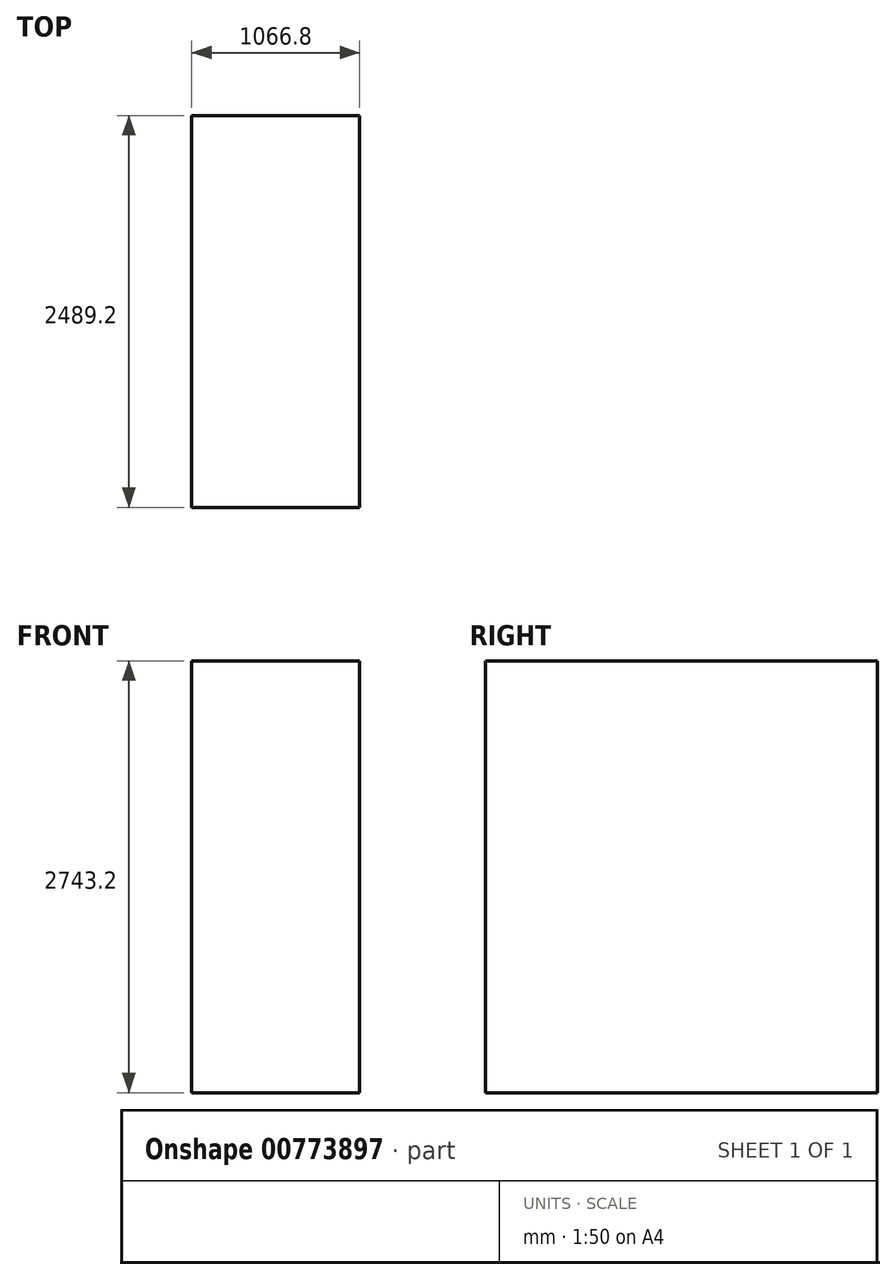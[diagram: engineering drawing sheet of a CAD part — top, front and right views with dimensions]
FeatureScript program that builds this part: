
annotation { "Feature Type Name" : "Feature", "Feature Type Description" : "" }
export const myFeature = defineFeature(function(context is Context, id is Id, definition is map)
    precondition{}
    {
        {
            var Q0;
            Q0=qCreatedBy(makeId("Front.planeOp"),FACE);
            var sketch = newSketch(context, id + "F0", { "sketchPlane" : qUnion([Q0])});
            skLineSegment(sketch, "E0", {"start": v(-539.32, 1878.52) * mm, "end": v(-539.32, -864.68) * mm});
            skLineSegment(sketch, "E1", {"start": v(-539.32, -864.68) * mm, "end": v(527.48, -864.68) * mm});
            skLineSegment(sketch, "E2", {"start": v(527.48, -864.68) * mm, "end": v(527.48, 1878.52) * mm});
            skLineSegment(sketch, "E3", {"start": v(527.48, 1878.52) * mm, "end": v(-539.32, 1878.52) * mm});
            skLineSegment(sketch, "E4", {"start": v(-539.32, 1878.52) * mm, "end": v(527.48, 1878.52) * mm});
            skSolve(sketch);
        }
        {
            var Q0;
            Q0 = qSketchRegion(id + "F0", true);
            extrude(context, id + "F1", {"entities" : qUnion([Q0]), "oppositeDirection" : true, "depth" : 2489.2 * mm, "offsetDistance" : 25.4 * mm});
        }
    });
